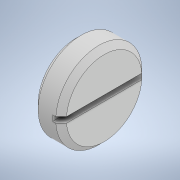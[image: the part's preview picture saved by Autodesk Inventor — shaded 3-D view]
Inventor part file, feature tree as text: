
AUTODESK INVENTOR PART (.ipt)
format: ipt  version: 2022 (Build 260153000, 153)  size: 173,056 bytes
history: native  units: mm
features: sketch x4, other x2, revolve x2, hole x1, extrude x1
ambient origin geometry x8: Origin, YZ Plane, XZ Plane, XY Plane, X Axis, Y Axis, Z Axis, Center Point
bodies: Body1 (feature_tree)
feature tree (10):
  other  "Твердое тело1"
  revolve  "Вращение1"
  hole  "Отверстие1"  [1 undecoded]
  revolve  "Вращение2"
  other  "РабПлоскость1"
  extrude  "Выдавливание1"  Depth=4.0mm
  sketch  "Эскиз1"
  sketch  "Эскиз2"
  sketch  "Эскиз3"
  sketch  "Эскиз4"
note: 1 required parameter value undecoded (feature->parameter linkage not recoverable at this tier; creation-order binding heuristic only, values carry confidence <= 0.55)
